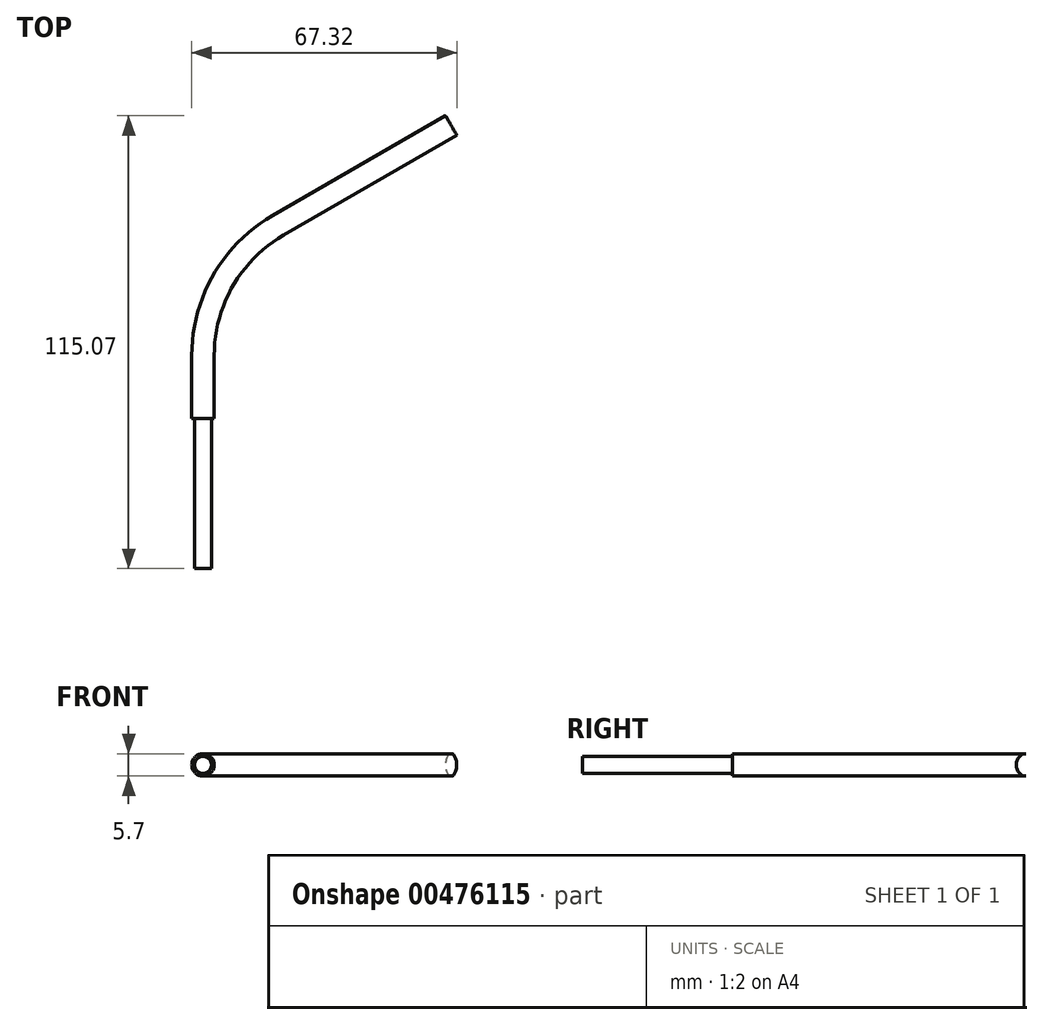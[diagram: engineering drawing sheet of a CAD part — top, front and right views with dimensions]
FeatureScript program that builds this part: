
annotation { "Feature Type Name" : "Feature", "Feature Type Description" : "" }
export const myFeature = defineFeature(function(context is Context, id is Id, definition is map)
    precondition{}
    {
        {
            var Q0;
            Q0=qCreatedBy(makeId("Top.planeOp"),FACE);
            var sketch = newSketch(context, id + "F0", { "sketchPlane" : qUnion([Q0])});
            skLineSegment(sketch, "E0", {"start": v(0, 0) * mm, "end": v(0, 16.1) * mm});
            skLineSegment(sketch, "E1", {"start": v(19.05, 49.1) * mm, "end": v(63.04, 74.5) * mm});
            skLineSegment(sketch, "E2", {"start": v(0, 0) * mm, "end": v(0, -38.1) * mm});
            skPoint(sketch, "E3.visualSharp", {"position": v(0, 38.1) * mm});
            skArc(sketch, "E3.filletArc", {"start": v(19.05, 49.1) * mm, "mid": v(5.1, 35.15) * mm, "end": v(0, 16.1) * mm});
            skPoint(sketch, "E4.visualSharp", {"position": v(175.98, 139.7) * mm});
            skSolve(sketch);
        }
        {
            var Q0;
            Q0=qCreatedBy(makeId("Front.planeOp"),FACE);
            var sketch = newSketch(context, id + "F1", { "sketchPlane" : qUnion([Q0])});
            skCircle(sketch, "E5", {"center": v(0, 0) * mm, "radius": 2.85 * mm});
            skSolve(sketch);
        }
        {
            var Q0;
            Q0=makeQuery(id+"F1.imprint","IMPRINT",FACE,{"disambiguationData":[TD([[makeQuery(id+"F1.imprint","IMPRINT",EDGE,{"derivedFrom":sQuery(id+"F1.wireOp",EDGE,"E5")}),1.0]])]});
            var Q1;
            Q1=sQuery(id+"F0.wireOp",EDGE,"E0");
            var Q2;
            Q2=sQuery(id+"F0.wireOp",EDGE,"E3.filletArc");
            var Q3;
            Q3=sQuery(id+"F0.wireOp",EDGE,"E1");
            var Q4;
            Q4=sQuery(id+"F0.wireOp",EDGE,"E4.filletArc");
            var Q5;
            Q5=sQuery(id+"F0.wireOp",EDGE,"lWv93iFz-bEN9-oXhL-jszu-YtIgDBo05eqF");
            var Q6;
            Q6=sQuery(id+"F0.wireOp",EDGE,"rNUARqjs-TsUK-Telz-jRy7-cFuhtV7gu0Rw");
            sweep(context, id + "F2", {"profiles" : qUnion([Q0]), "path" : qUnion([Q1, Q2, Q3, Q4, Q5, Q6])});
        }
        {
            var Q0;
            Q0 = qSketchRegion(id + "F1", true);
            var Q1;
            Q1=sQuery(id+"F0.wireOp",EDGE,"E2");
            sweep(context, id + "F3", {"operationType" : NewBodyOperationType.ADD, "profiles" : qUnion([Q0]), "path" : qUnion([Q1])});
        }
        {
            var Q0;
            Q0=makeQuery(id+"F3.opSweep","CAP_FACE",FACE,{"disambiguationData":[OSD([sQuery(id+"F0.wireOp",VERTEX,"E2.end"),sQuery(id+"F1.wireOp",EDGE,"E5")])],"isStart":false});
            var sketch = newSketch(context, id + "F4", { "sketchPlane" : qUnion([Q0])});
            skCircle(sketch, "E6", {"center": v(0, 0) * mm, "radius": 2.15 * mm});
            skCircle(sketch, "E7", {"center": v(0, 0) * mm, "radius": 2.85 * mm});
            skSolve(sketch);
        }
        {
            var Q0;
            Q0=makeQuery(id+"F4.imprint","IMPRINT",FACE,{"disambiguationData":[TD([[makeQuery(id+"F4.imprint","IMPRINT",EDGE,{"derivedFrom":sQuery(id+"F4.wireOp",EDGE,"E6")}),-1.0]])]});
            extrude(context, id + "F5", {"entities" : qUnion([Q0]), "operationType" : NewBodyOperationType.REMOVE, "oppositeDirection" : true, "depth" : 38.1 * mm});
        }
    });
